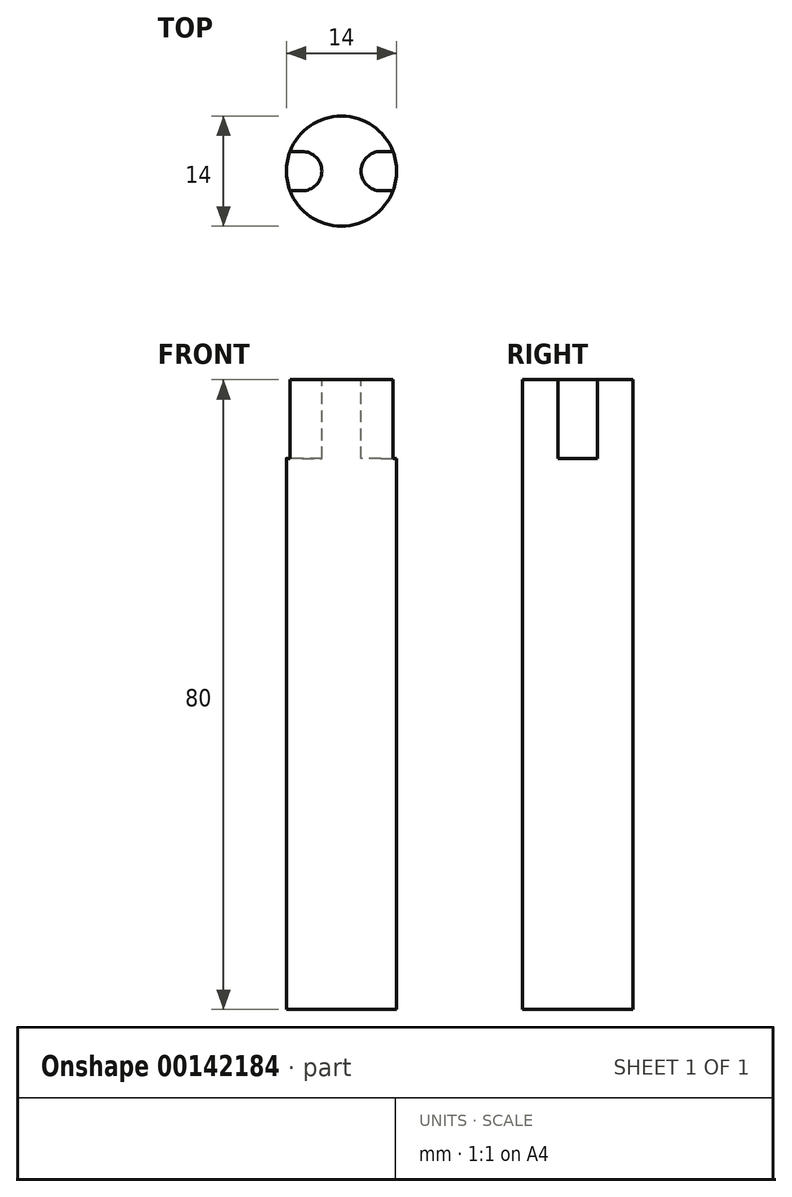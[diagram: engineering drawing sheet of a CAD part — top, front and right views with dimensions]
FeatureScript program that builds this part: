
annotation { "Feature Type Name" : "Feature", "Feature Type Description" : "" }
export const myFeature = defineFeature(function(context is Context, id is Id, definition is map)
    precondition{}
    {
        {
            var Q0;
            Q0=qCreatedBy(makeId("Top.planeOp"),FACE);
            var sketch = newSketch(context, id + "F0", { "sketchPlane" : qUnion([Q0])});
            skCircle(sketch, "E0", {"center": v(0, 0) * mm, "radius": 7 * mm});
            skSolve(sketch);
        }
        {
            var Q0;
            Q0=makeQuery(id+"F0.imprint","IMPRINT",FACE,{"disambiguationData":[TD([[makeQuery(id+"F0.imprint","IMPRINT",EDGE,{"derivedFrom":sQuery(id+"F0.wireOp",EDGE,"E0")}),1.0]])]});
            extrude(context, id + "F1", {"entities" : qUnion([Q0]), "depth" : 80 * mm});
        }
        {
            var Q0;
            Q0=makeQuery(id+"F1.opExtrude","CAP_FACE",FACE,{"disambiguationData":[OSD([sQuery(id+"F0.wireOp",EDGE,"E0")])],"isStart":false});
            var sketch = newSketch(context, id + "F2", { "sketchPlane" : qUnion([Q0])});
            skArc(sketch, "E1", {"start": v(-5, -2.5) * mm, "mid": v(-2.5, 0) * mm, "end": v(-4.99, 2.5) * mm});
            skArc(sketch, "E2", {"start": v(5, 2.5) * mm, "mid": v(2.5, 0) * mm, "end": v(5, -2.5) * mm});
            skLineSegment(sketch, "E3", {"start": v(-4.99, 2.5) * mm, "end": v(-6.54, 2.5) * mm});
            skLineSegment(sketch, "E4", {"start": v(-5, -2.5) * mm, "end": v(-6.54, -2.5) * mm});
            skLineSegment(sketch, "E5", {"start": v(5, 2.5) * mm, "end": v(6.54, 2.5) * mm});
            skLineSegment(sketch, "E6", {"start": v(5, -2.5) * mm, "end": v(6.54, -2.5) * mm});
            skSolve(sketch);
        }
        {
            var Q0;
            Q0=makeQuery(id+"F2.imprint","IMPRINT",FACE,{"disambiguationData":[TD([[makeQuery(id+"F2.imprint","IMPRINT",EDGE,{"derivedFrom":sQuery(id+"F2.wireOp",EDGE,"E1")}),1.0]])]});
            var Q1;
            Q1=makeQuery(id+"F2.imprint","IMPRINT",FACE,{"disambiguationData":[TD([[makeQuery(id+"F2.imprint","IMPRINT",EDGE,{"derivedFrom":sQuery(id+"F2.wireOp",EDGE,"E2")}),1.0]])]});
            extrude(context, id + "F3", {"entities" : qUnion([Q0, Q1]), "operationType" : NewBodyOperationType.REMOVE, "oppositeDirection" : true, "depth" : 10 * mm});
        }
    });
